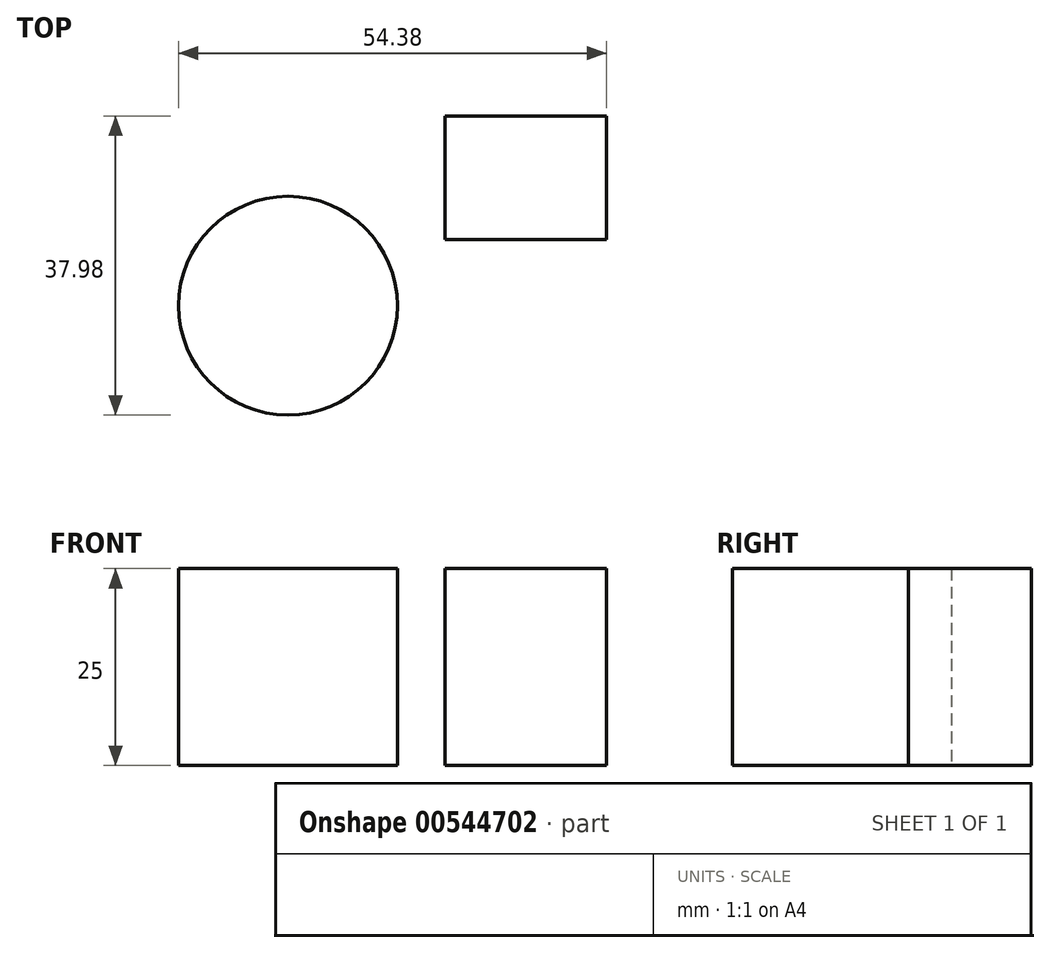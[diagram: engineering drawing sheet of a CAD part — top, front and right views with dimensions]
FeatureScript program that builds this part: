
annotation { "Feature Type Name" : "Feature", "Feature Type Description" : "" }
export const myFeature = defineFeature(function(context is Context, id is Id, definition is map)
    precondition{}
    {
        {
            var Q0;
            Q0=qCreatedBy(makeId("Top.planeOp"),FACE);
            var sketch = newSketch(context, id + "F0", { "sketchPlane" : qUnion([Q0])});
            skLineSegment(sketch, "E0.bottom", {"start": v(10.26, -7.84) * mm, "end": v(-10.26, -7.84) * mm});
            skLineSegment(sketch, "E0.top", {"start": v(10.26, 7.84) * mm, "end": v(-10.26, 7.84) * mm});
            skLineSegment(sketch, "E0.left", {"start": v(10.26, -7.84) * mm, "end": v(10.26, 7.84) * mm});
            skLineSegment(sketch, "E0.right", {"start": v(-10.26, -7.84) * mm, "end": v(-10.26, 7.84) * mm});
            skPoint(sketch, "E0.middle", {"position": v(0, 0) * mm});
            skSolve(sketch);
        }
        {
            var Q0;
            Q0=makeQuery(id+"F0.imprint","IMPRINT",FACE,{"disambiguationData":[TD([[makeQuery(id+"F0.imprint","IMPRINT",EDGE,{"derivedFrom":sQuery(id+"F0.wireOp",EDGE,"E0.bottom")}),-1.0]])]});
            extrude(context, id + "F1", {"entities" : qUnion([Q0]), "depth" : 25 * mm, "offsetDistance" : 25 * mm});
        }
        {
            var Q0;
            Q0=qCreatedBy(makeId("Top.planeOp"),FACE);
            var sketch = newSketch(context, id + "F2", { "sketchPlane" : qUnion([Q0])});
            skCircle(sketch, "E1", {"center": v(-30.22, -16.24) * mm, "radius": 13.9 * mm});
            skSolve(sketch);
        }
        {
            var Q0;
            Q0=makeQuery(id+"F2.imprint","IMPRINT",FACE,{"disambiguationData":[TD([[makeQuery(id+"F2.imprint","IMPRINT",EDGE,{"derivedFrom":sQuery(id+"F2.wireOp",EDGE,"E1")}),1.0]])]});
            extrude(context, id + "F3", {"entities" : qUnion([Q0]), "depth" : 25 * mm, "offsetDistance" : 25 * mm});
        }
    });
